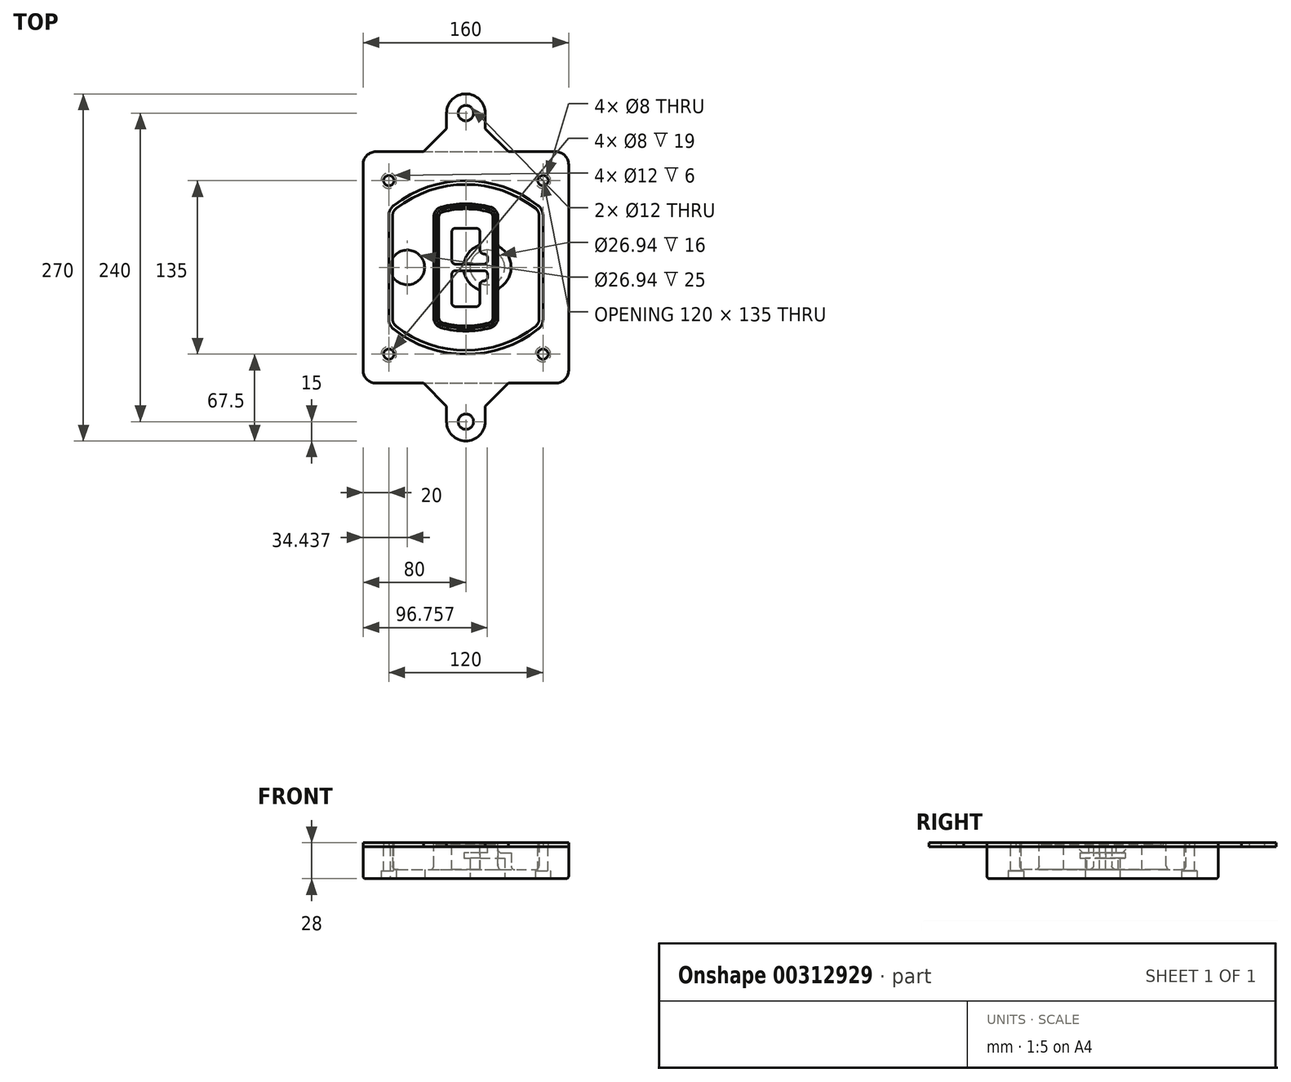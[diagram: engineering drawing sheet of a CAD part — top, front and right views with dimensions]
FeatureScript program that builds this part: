
annotation { "Feature Type Name" : "Feature", "Feature Type Description" : "" }
export const myFeature = defineFeature(function(context is Context, id is Id, definition is map)
    precondition{}
    {
        {
            var Q0;
            Q0=qCreatedBy(makeId("Top.planeOp"),FACE);
            var sketch = newSketch(context, id + "F0", { "sketchPlane" : qUnion([Q0])});
            skPoint(sketch, "E0.rect.middle", {"position": v(0, 0) * mm});
            skLineSegment(sketch, "E1.bottom", {"start": v(-70, -90) * mm, "end": v(70, -90) * mm});
            skLineSegment(sketch, "E1.top", {"start": v(-70, 90) * mm, "end": v(70, 90) * mm});
            skLineSegment(sketch, "E1.left", {"start": v(-80, -80) * mm, "end": v(-80, 80) * mm});
            skLineSegment(sketch, "E1.right", {"start": v(80, -80) * mm, "end": v(80, 80) * mm});
            skLineSegment(sketch, "E2", {"start": v(-80, 90) * mm, "end": v(80, -90) * mm, "construction": true});
            skLineSegment(sketch, "E3", {"start": v(80, 90) * mm, "end": v(-80, -90) * mm, "construction": true});
            skCircle(sketch, "E4", {"center": v(-60, 67.5) * mm, "radius": 4 * mm});
            skCircle(sketch, "E5", {"center": v(60, 67.5) * mm, "radius": 4 * mm});
            skCircle(sketch, "E6", {"center": v(60, -67.5) * mm, "radius": 4 * mm});
            skCircle(sketch, "E7", {"center": v(-60, -67.5) * mm, "radius": 4 * mm});
            skLineSegment(sketch, "E8", {"start": v(-60, 67.5) * mm, "end": v(60, 67.5) * mm, "construction": true});
            skLineSegment(sketch, "E9", {"start": v(60, 67.5) * mm, "end": v(60, -67.5) * mm, "construction": true});
            skLineSegment(sketch, "E10", {"start": v(60, -67.5) * mm, "end": v(-60, -67.5) * mm, "construction": true});
            skLineSegment(sketch, "E11", {"start": v(-60, -67.5) * mm, "end": v(-60, 67.5) * mm, "construction": true});
            skLineSegment(sketch, "E12", {"start": v(-60, 40.3) * mm, "end": v(-60, -40.3) * mm});
            skLineSegment(sketch, "E13", {"start": v(60, 40.3) * mm, "end": v(60, -40.3) * mm});
            skArc(sketch, "E14", {"start": v(56.15, 48.18) * mm, "mid": v(0, 67.5) * mm, "end": v(-56.15, 48.18) * mm});
            skArc(sketch, "E15", {"start": v(-56.15, -48.18) * mm, "mid": v(0, -67.5) * mm, "end": v(56.15, -48.18) * mm});
            skLineSegment(sketch, "E16", {"start": v(-60, 0) * mm, "end": v(60, 0) * mm, "construction": true});
            skPoint(sketch, "E17.visualSharp", {"position": v(-60, -45) * mm});
            skArc(sketch, "E17.filletArc", {"start": v(-60, -40.3) * mm, "mid": v(-58.99, -44.68) * mm, "end": v(-56.15, -48.18) * mm});
            skPoint(sketch, "E18.visualSharp", {"position": v(-60, 45) * mm});
            skArc(sketch, "E18.filletArc", {"start": v(-56.15, 48.18) * mm, "mid": v(-58.99, 44.68) * mm, "end": v(-60, 40.3) * mm});
            skPoint(sketch, "E19.visualSharp", {"position": v(60, 45) * mm});
            skArc(sketch, "E19.filletArc", {"start": v(60, 40.3) * mm, "mid": v(58.99, 44.68) * mm, "end": v(56.15, 48.18) * mm});
            skPoint(sketch, "E20.visualSharp", {"position": v(60, -45) * mm});
            skArc(sketch, "E20.filletArc", {"start": v(56.15, -48.18) * mm, "mid": v(58.99, -44.68) * mm, "end": v(60, -40.3) * mm});
            skPoint(sketch, "E21.visualSharp", {"position": v(-80, 90) * mm});
            skArc(sketch, "E21.filletArc", {"start": v(-70, 90) * mm, "mid": v(-77.07, 87.07) * mm, "end": v(-80, 80) * mm});
            skPoint(sketch, "E22.visualSharp", {"position": v(80, 90) * mm});
            skArc(sketch, "E22.filletArc", {"start": v(80, 80) * mm, "mid": v(77.07, 87.07) * mm, "end": v(70, 90) * mm});
            skPoint(sketch, "E23.visualSharp", {"position": v(80, -90) * mm});
            skArc(sketch, "E23.filletArc", {"start": v(70, -90) * mm, "mid": v(77.07, -87.07) * mm, "end": v(80, -80) * mm});
            skPoint(sketch, "E24.visualSharp", {"position": v(-80, -90) * mm});
            skArc(sketch, "E24.filletArc", {"start": v(-80, -80) * mm, "mid": v(-77.07, -87.07) * mm, "end": v(-70, -90) * mm});
            skArc(sketch, "E25.0", {"start": v(57, 40.3) * mm, "mid": v(56.3, 43.36) * mm, "end": v(54.3, 45.81) * mm});
            skLineSegment(sketch, "E25.1", {"start": v(57, 40.3) * mm, "end": v(57, -40.3) * mm});
            skArc(sketch, "E25.2", {"start": v(54.3, -45.81) * mm, "mid": v(56.3, -43.36) * mm, "end": v(57, -40.3) * mm});
            skArc(sketch, "E25.3", {"start": v(-54.3, -45.81) * mm, "mid": v(0, -64.5) * mm, "end": v(54.3, -45.81) * mm});
            skArc(sketch, "E25.4", {"start": v(-57, -40.3) * mm, "mid": v(-56.3, -43.36) * mm, "end": v(-54.3, -45.81) * mm});
            skArc(sketch, "E25.5", {"start": v(54.3, 45.81) * mm, "mid": v(0, 64.5) * mm, "end": v(-54.3, 45.81) * mm});
            skLineSegment(sketch, "E25.6", {"start": v(-57, 40.3) * mm, "end": v(-57, -40.3) * mm});
            skArc(sketch, "E25.7", {"start": v(-54.3, 45.81) * mm, "mid": v(-56.3, 43.36) * mm, "end": v(-57, 40.3) * mm});
            skArc(sketch, "E26.0", {"start": v(-58.62, 51.33) * mm, "mid": v(-62.58, 46.43) * mm, "end": v(-64, 40.3) * mm});
            skArc(sketch, "E26.1", {"start": v(58.62, 51.33) * mm, "mid": v(0, 71.5) * mm, "end": v(-58.62, 51.33) * mm});
            skArc(sketch, "E26.2", {"start": v(64, 40.3) * mm, "mid": v(62.58, 46.43) * mm, "end": v(58.62, 51.33) * mm});
            skLineSegment(sketch, "E26.3", {"start": v(64, 40.3) * mm, "end": v(64, -40.3) * mm});
            skArc(sketch, "E26.4", {"start": v(58.62, -51.33) * mm, "mid": v(62.58, -46.43) * mm, "end": v(64, -40.3) * mm});
            skLineSegment(sketch, "E26.5", {"start": v(-64, 40.3) * mm, "end": v(-64, -40.3) * mm});
            skArc(sketch, "E26.6", {"start": v(-58.62, -51.33) * mm, "mid": v(0, -71.5) * mm, "end": v(58.62, -51.33) * mm});
            skArc(sketch, "E26.7", {"start": v(-64, -40.3) * mm, "mid": v(-62.58, -46.43) * mm, "end": v(-58.62, -51.33) * mm});
            skSolve(sketch);
        }
        {
            var Q0;
            Q0=makeQuery(id+"F0.imprint","IMPRINT",FACE,{"disambiguationData":[TD([[makeQuery(id+"F0.imprint","IMPRINT",EDGE,{"derivedFrom":sQuery(id+"F0.wireOp",EDGE,"E1.bottom")}),1.0]])]});
            var Q1;
            Q1=makeQuery(id+"F0.imprint","IMPRINT",FACE,{"disambiguationData":[TD([[makeQuery(id+"F0.imprint","IMPRINT",EDGE,{"derivedFrom":sQuery(id+"F0.wireOp",EDGE,"E12")}),1.0]])]});
            var Q2;
            Q2=makeQuery(id+"F0.imprint","IMPRINT",FACE,{"disambiguationData":[TD([[makeQuery(id+"F0.imprint","IMPRINT",EDGE,{"derivedFrom":sQuery(id+"F0.wireOp",EDGE,"E25.0")}),1.0]])]});
            var Q3;
            Q3=makeQuery(id+"F0.imprint","IMPRINT",FACE,{"disambiguationData":[TD([[makeQuery(id+"F0.imprint","IMPRINT",EDGE,{"derivedFrom":sQuery(id+"F0.wireOp",EDGE,"E12")}),-1.0]])]});
            extrude(context, id + "F1", {"entities" : qUnion([Q0, Q1, Q2, Q3]), "oppositeDirection" : true, "depth" : 25 * mm});
        }
        {
            var Q0;
            Q0=makeQuery(id+"F0.imprint","IMPRINT",FACE,{"disambiguationData":[TD([[makeQuery(id+"F0.imprint","IMPRINT",EDGE,{"derivedFrom":sQuery(id+"F0.wireOp",EDGE,"E12")}),1.0]])]});
            extrude(context, id + "F2", {"entities" : qUnion([Q0]), "operationType" : NewBodyOperationType.ADD, "depth" : 3 * mm});
        }
        {
            var Q0;
            Q0=makeQuery(id+"F0.imprint","IMPRINT",FACE,{"disambiguationData":[TD([[makeQuery(id+"F0.imprint","IMPRINT",EDGE,{"derivedFrom":sQuery(id+"F0.wireOp",EDGE,"E25.0")}),1.0]])]});
            extrude(context, id + "F3", {"entities" : qUnion([Q0]), "operationType" : NewBodyOperationType.REMOVE, "oppositeDirection" : true, "depth" : 18 * mm});
        }
        {
            var Q0;
            Q0=makeQuery(id+"F2.opExtrude","CAP_FACE",FACE,{"disambiguationData":[OSD([sQuery(id+"F0.wireOp",EDGE,"E12"),sQuery(id+"F0.wireOp",EDGE,"E13"),sQuery(id+"F0.wireOp",EDGE,"E14"),sQuery(id+"F0.wireOp",EDGE,"E15"),sQuery(id+"F0.wireOp",EDGE,"E17.filletArc"),sQuery(id+"F0.wireOp",EDGE,"E18.filletArc"),sQuery(id+"F0.wireOp",EDGE,"E19.filletArc"),sQuery(id+"F0.wireOp",EDGE,"E20.filletArc"),sQuery(id+"F0.wireOp",EDGE,"E25.0"),sQuery(id+"F0.wireOp",EDGE,"E25.1"),sQuery(id+"F0.wireOp",EDGE,"E25.2"),sQuery(id+"F0.wireOp",EDGE,"E25.3"),sQuery(id+"F0.wireOp",EDGE,"E25.4"),sQuery(id+"F0.wireOp",EDGE,"E25.5"),sQuery(id+"F0.wireOp",EDGE,"E25.6"),sQuery(id+"F0.wireOp",EDGE,"E25.7")])],"isStart":false});
            var sketch = newSketch(context, id + "F4", { "sketchPlane" : qUnion([Q0])});
            skArc(sketch, "E27.0", {"start": v(-19.08, -46.97) * mm, "mid": v(0, -49.5) * mm, "end": v(19.08, -46.97) * mm});
            skArc(sketch, "E28.0", {"start": v(19.08, 46.97) * mm, "mid": v(0, 49.5) * mm, "end": v(-19.08, 46.97) * mm});
            skLineSegment(sketch, "E29", {"start": v(-25, 39.25) * mm, "end": v(-25, -39.25) * mm});
            skLineSegment(sketch, "E30", {"start": v(25, 39.25) * mm, "end": v(25, -39.25) * mm});
            skLineSegment(sketch, "E31", {"start": v(-25, 45.1) * mm, "end": v(25, 45.1) * mm, "construction": true});
            skLineSegment(sketch, "E32", {"start": v(-25, -45.1) * mm, "end": v(25, -45.1) * mm, "construction": true});
            skPoint(sketch, "E33.visualSharp", {"position": v(-25, 45.1) * mm});
            skArc(sketch, "E33.filletArc", {"start": v(-19.08, 46.97) * mm, "mid": v(-23.35, 44.11) * mm, "end": v(-25, 39.25) * mm});
            skPoint(sketch, "E34.visualSharp", {"position": v(25, 45.1) * mm});
            skArc(sketch, "E34.filletArc", {"start": v(25, 39.25) * mm, "mid": v(23.35, 44.11) * mm, "end": v(19.08, 46.97) * mm});
            skPoint(sketch, "E35.visualSharp", {"position": v(25, -45.1) * mm});
            skArc(sketch, "E35.filletArc", {"start": v(19.08, -46.97) * mm, "mid": v(23.35, -44.11) * mm, "end": v(25, -39.25) * mm});
            skPoint(sketch, "E36.visualSharp", {"position": v(-25, -45.1) * mm});
            skArc(sketch, "E36.filletArc", {"start": v(-25, -39.25) * mm, "mid": v(-23.35, -44.11) * mm, "end": v(-19.08, -46.97) * mm});
            skArc(sketch, "E37.0", {"start": v(54.3, 45.81) * mm, "mid": v(0, 64.5) * mm, "end": v(-54.3, 45.81) * mm});
            skArc(sketch, "E37.1", {"start": v(-54.3, 45.81) * mm, "mid": v(-56.3, 43.36) * mm, "end": v(-57, 40.3) * mm});
            skLineSegment(sketch, "E37.2", {"start": v(-57, 40.3) * mm, "end": v(-57, -40.3) * mm});
            skArc(sketch, "E37.3", {"start": v(-57, -40.3) * mm, "mid": v(-56.3, -43.36) * mm, "end": v(-54.3, -45.81) * mm});
            skArc(sketch, "E37.4", {"start": v(-54.3, -45.81) * mm, "mid": v(0, -64.5) * mm, "end": v(54.3, -45.81) * mm});
            skArc(sketch, "E37.5", {"start": v(54.3, -45.81) * mm, "mid": v(56.3, -43.36) * mm, "end": v(57, -40.3) * mm});
            skLineSegment(sketch, "E37.6", {"start": v(57, 40.3) * mm, "end": v(57, -40.3) * mm});
            skArc(sketch, "E37.7", {"start": v(57, 40.3) * mm, "mid": v(56.3, 43.36) * mm, "end": v(54.3, 45.81) * mm});
            skLineSegment(sketch, "E38.0", {"start": v(23, 39.25) * mm, "end": v(23, -39.25) * mm});
            skArc(sketch, "E38.1", {"start": v(18.56, -45.04) * mm, "mid": v(21.76, -42.9) * mm, "end": v(23, -39.25) * mm});
            skArc(sketch, "E38.2", {"start": v(-18.56, -45.04) * mm, "mid": v(0, -47.5) * mm, "end": v(18.56, -45.04) * mm});
            skArc(sketch, "E38.3", {"start": v(-23, -39.25) * mm, "mid": v(-21.76, -42.9) * mm, "end": v(-18.56, -45.04) * mm});
            skLineSegment(sketch, "E38.4", {"start": v(-23, 39.25) * mm, "end": v(-23, -39.25) * mm});
            skArc(sketch, "E38.5", {"start": v(23, 39.25) * mm, "mid": v(21.76, 42.9) * mm, "end": v(18.56, 45.04) * mm});
            skArc(sketch, "E38.6", {"start": v(-18.56, 45.04) * mm, "mid": v(-21.76, 42.9) * mm, "end": v(-23, 39.25) * mm});
            skArc(sketch, "E38.7", {"start": v(18.56, 45.04) * mm, "mid": v(0, 47.5) * mm, "end": v(-18.56, 45.04) * mm});
            skArc(sketch, "E39.0", {"start": v(21, 39.25) * mm, "mid": v(20.18, 41.68) * mm, "end": v(18.04, 43.1) * mm});
            skLineSegment(sketch, "E39.1", {"start": v(21, 39.25) * mm, "end": v(21, -39.25) * mm});
            skArc(sketch, "E39.2", {"start": v(18.04, -43.1) * mm, "mid": v(20.18, -41.68) * mm, "end": v(21, -39.25) * mm});
            skArc(sketch, "E39.3", {"start": v(-18.04, -43.1) * mm, "mid": v(0, -45.5) * mm, "end": v(18.04, -43.1) * mm});
            skArc(sketch, "E39.4", {"start": v(-21, -39.25) * mm, "mid": v(-20.18, -41.68) * mm, "end": v(-18.04, -43.1) * mm});
            skArc(sketch, "E39.5", {"start": v(18.04, 43.1) * mm, "mid": v(0, 45.5) * mm, "end": v(-18.04, 43.1) * mm});
            skLineSegment(sketch, "E39.6", {"start": v(-21, 39.25) * mm, "end": v(-21, -39.25) * mm});
            skArc(sketch, "E39.7", {"start": v(-18.04, 43.1) * mm, "mid": v(-20.18, 41.68) * mm, "end": v(-21, 39.25) * mm});
            skLineSegment(sketch, "E40", {"start": v(-25, 0) * mm, "end": v(25, 0) * mm, "construction": true});
            skLineSegment(sketch, "E41", {"start": v(-11, 5.5) * mm, "end": v(-11, 27.5) * mm});
            skLineSegment(sketch, "E42", {"start": v(-8, 30.5) * mm, "end": v(8, 30.5) * mm});
            skLineSegment(sketch, "E43", {"start": v(11, 27.5) * mm, "end": v(11, 13.5) * mm});
            skLineSegment(sketch, "E44", {"start": v(14, 10.5) * mm, "end": v(14, 10.5) * mm});
            skLineSegment(sketch, "E45", {"start": v(17, 7.5) * mm, "end": v(17, 5.5) * mm});
            skLineSegment(sketch, "E46", {"start": v(14, 2.5) * mm, "end": v(-8, 2.5) * mm});
            skPoint(sketch, "E47.visualSharp", {"position": v(-11, 30.5) * mm});
            skArc(sketch, "E47.filletArc", {"start": v(-8, 30.5) * mm, "mid": v(-10.12, 29.62) * mm, "end": v(-11, 27.5) * mm});
            skPoint(sketch, "E48.visualSharp", {"position": v(11, 30.5) * mm});
            skArc(sketch, "E48.filletArc", {"start": v(11, 27.5) * mm, "mid": v(10.12, 29.62) * mm, "end": v(8, 30.5) * mm});
            skPoint(sketch, "E49.visualSharp", {"position": v(11, 10.5) * mm});
            skArc(sketch, "E49.filletArc", {"start": v(11, 13.5) * mm, "mid": v(11.88, 11.38) * mm, "end": v(14, 10.5) * mm});
            skPoint(sketch, "E50.visualSharp", {"position": v(17, 10.5) * mm});
            skArc(sketch, "E50.filletArc", {"start": v(17, 7.5) * mm, "mid": v(16.12, 9.62) * mm, "end": v(14, 10.5) * mm});
            skPoint(sketch, "E51.visualSharp", {"position": v(17, 2.5) * mm});
            skArc(sketch, "E51.filletArc", {"start": v(14, 2.5) * mm, "mid": v(16.12, 3.38) * mm, "end": v(17, 5.5) * mm});
            skPoint(sketch, "E52.visualSharp", {"position": v(-11, 2.5) * mm});
            skArc(sketch, "E52.filletArc", {"start": v(-11, 5.5) * mm, "mid": v(-10.12, 3.38) * mm, "end": v(-8, 2.5) * mm});
            skLineSegment(sketch, "E53.0.MirrorCS", {"start": v(14, -2.5) * mm, "end": v(-8, -2.5) * mm});
            skArc(sketch, "E54.0.MirrorCS", {"start": v(-11, -5.5) * mm, "mid": v(-10.12, -3.38) * mm, "end": v(-8, -2.5) * mm});
            skLineSegment(sketch, "E55.0.MirrorCS", {"start": v(-11, -5.5) * mm, "end": v(-11, -27.5) * mm});
            skArc(sketch, "E56.0.MirrorCS", {"start": v(-8, -30.5) * mm, "mid": v(-10.12, -29.62) * mm, "end": v(-11, -27.5) * mm});
            skLineSegment(sketch, "E57.0.MirrorCS", {"start": v(-8, -30.5) * mm, "end": v(8, -30.5) * mm});
            skArc(sketch, "E58.0.MirrorCS", {"start": v(11, -27.5) * mm, "mid": v(10.12, -29.62) * mm, "end": v(8, -30.5) * mm});
            skLineSegment(sketch, "E59.0.MirrorCS", {"start": v(11, -27.5) * mm, "end": v(11, -13.5) * mm});
            skArc(sketch, "E60.0.MirrorCS", {"start": v(11, -13.5) * mm, "mid": v(11.88, -11.38) * mm, "end": v(14, -10.5) * mm});
            skArc(sketch, "E61.0.MirrorCS", {"start": v(17, -7.5) * mm, "mid": v(16.12, -9.62) * mm, "end": v(14, -10.5) * mm});
            skLineSegment(sketch, "E62.0.MirrorCS", {"start": v(17, -7.5) * mm, "end": v(17, -5.5) * mm});
            skArc(sketch, "E63.0.MirrorCS", {"start": v(14, -2.5) * mm, "mid": v(16.12, -3.38) * mm, "end": v(17, -5.5) * mm});
            skSolve(sketch);
        }
        {
            var Q0;
            Q0=makeQuery(id+"F4.imprint","IMPRINT",FACE,{"disambiguationData":[TD([[makeQuery(id+"F4.imprint","IMPRINT",EDGE,{"derivedFrom":sQuery(id+"F4.wireOp",EDGE,"E27.0")}),1.0]])]});
            var Q1;
            Q1=makeQuery(id+"F4.imprint","IMPRINT",FACE,{"disambiguationData":[TD([[makeQuery(id+"F4.imprint","IMPRINT",EDGE,{"derivedFrom":sQuery(id+"F4.wireOp",EDGE,"E38.0")}),-1.0]])]});
            var Q2;
            Q2=makeQuery(id+"F4.imprint","IMPRINT",FACE,{"disambiguationData":[TD([[makeQuery(id+"F4.imprint","IMPRINT",EDGE,{"derivedFrom":sQuery(id+"F4.wireOp",EDGE,"E39.0")}),1.0]])]});
            extrude(context, id + "F5", {"entities" : qUnion([Q0, Q1, Q2]), "operationType" : NewBodyOperationType.ADD, "endBound" : BoundingType.UP_TO_NEXT, "oppositeDirection" : true, "depth" : 25 * mm});
        }
        {
            var Q0;
            Q0=makeQuery(id+"F4.imprint","IMPRINT",FACE,{"disambiguationData":[TD([[makeQuery(id+"F4.imprint","IMPRINT",EDGE,{"derivedFrom":sQuery(id+"F4.wireOp",EDGE,"E38.0")}),-1.0]])]});
            extrude(context, id + "F6", {"entities" : qUnion([Q0]), "operationType" : NewBodyOperationType.REMOVE, "oppositeDirection" : true, "depth" : 2 * mm});
        }
        {
            var Q0;
            Q0=makeQuery(id+"F1.opExtrude","CAP_FACE",FACE,{"disambiguationData":[OSD([sQuery(id+"F0.wireOp",EDGE,"E1.bottom"),sQuery(id+"F0.wireOp",EDGE,"E1.top"),sQuery(id+"F0.wireOp",EDGE,"E1.left"),sQuery(id+"F0.wireOp",EDGE,"E1.right"),sQuery(id+"F0.wireOp",EDGE,"E4"),sQuery(id+"F0.wireOp",EDGE,"E5"),sQuery(id+"F0.wireOp",EDGE,"E6"),sQuery(id+"F0.wireOp",EDGE,"E7"),sQuery(id+"F0.wireOp",EDGE,"E21.filletArc"),sQuery(id+"F0.wireOp",EDGE,"E22.filletArc"),sQuery(id+"F0.wireOp",EDGE,"E23.filletArc"),sQuery(id+"F0.wireOp",EDGE,"E24.filletArc")])],"isStart":false});
            var sketch = newSketch(context, id + "F7", { "sketchPlane" : qUnion([Q0])});
            skCircle(sketch, "E64", {"center": v(16.76, 0) * mm, "radius": 13.47 * mm});
            skCircle(sketch, "E65", {"center": v(-45.56, 0) * mm, "radius": 13.47 * mm});
            skLineSegment(sketch, "E66", {"start": v(80, 0) * mm, "end": v(-80, 0) * mm});
            skCircle(sketch, "E67", {"center": v(16.76, 0) * mm, "radius": 18.47 * mm});
            skCircle(sketch, "E68", {"center": v(60, -67.5) * mm, "radius": 6 * mm});
            skCircle(sketch, "E69", {"center": v(-60, -67.5) * mm, "radius": 6 * mm});
            skCircle(sketch, "E70", {"center": v(-60, 67.5) * mm, "radius": 6 * mm});
            skCircle(sketch, "E71", {"center": v(60, 67.5) * mm, "radius": 6 * mm});
            skSolve(sketch);
        }
        {
            var Q0;
            {var subQ1=sQuery(id+"F7.wireOp",EDGE,"E66");var subQ4=sQuery(id+"F7.wireOp",EDGE,"E64");var subQ6=makeQuery(id+"F7.imprint","INTERSECT",VERTEX,{"disambiguationData":[OD(0.0)],"derivedFrom":[subQ4,subQ1]});Q0=makeQuery(id+"F7.imprint","IMPRINT",FACE,{"disambiguationData":[TD([[makeQuery(id+"F7.imprint","IMPRINT",EDGE,{"disambiguationData":[TD([[subQ6,-1.0]])],"derivedFrom":subQ4}),-1.0]])]});}
            var Q1;
            {var subQ0=sQuery(id+"F7.wireOp",EDGE,"E66");var subQ1=sQuery(id+"F7.wireOp",EDGE,"E64");var subQ3=makeQuery(id+"F7.imprint","INTERSECT",VERTEX,{"disambiguationData":[OD(0.0)],"derivedFrom":[subQ1,subQ0]});Q1=makeQuery(id+"F7.imprint","IMPRINT",FACE,{"disambiguationData":[TD([[makeQuery(id+"F7.imprint","IMPRINT",EDGE,{"disambiguationData":[TD([[subQ3,-1.0]])],"derivedFrom":subQ1}),1.0]])]});}
            var Q2;
            {var subQ0=sQuery(id+"F7.wireOp",EDGE,"E66");var subQ1=sQuery(id+"F7.wireOp",EDGE,"E64");var subQ3=makeQuery(id+"F7.imprint","INTERSECT",VERTEX,{"disambiguationData":[OD(0.0)],"derivedFrom":[subQ1,subQ0]});Q2=makeQuery(id+"F7.imprint","IMPRINT",FACE,{"disambiguationData":[TD([[makeQuery(id+"F7.imprint","IMPRINT",EDGE,{"disambiguationData":[TD([[subQ3,1.0]])],"derivedFrom":subQ1}),1.0]])]});}
            var Q3;
            {var subQ1=sQuery(id+"F7.wireOp",EDGE,"E66");var subQ4=sQuery(id+"F7.wireOp",EDGE,"E64");var subQ6=makeQuery(id+"F7.imprint","INTERSECT",VERTEX,{"disambiguationData":[OD(0.0)],"derivedFrom":[subQ4,subQ1]});Q3=makeQuery(id+"F7.imprint","IMPRINT",FACE,{"disambiguationData":[TD([[makeQuery(id+"F7.imprint","IMPRINT",EDGE,{"disambiguationData":[TD([[subQ6,1.0]])],"derivedFrom":subQ4}),-1.0]])]});}
            extrude(context, id + "F8", {"entities" : qUnion([Q0, Q1, Q2, Q3]), "operationType" : NewBodyOperationType.ADD, "oppositeDirection" : true, "depth" : 20 * mm});
        }
        {
            var Q0;
            {var subQ0=sQuery(id+"F7.wireOp",EDGE,"E66");var subQ1=sQuery(id+"F7.wireOp",EDGE,"E64");var subQ3=makeQuery(id+"F7.imprint","INTERSECT",VERTEX,{"disambiguationData":[OD(0.0)],"derivedFrom":[subQ1,subQ0]});Q0=makeQuery(id+"F7.imprint","IMPRINT",FACE,{"disambiguationData":[TD([[makeQuery(id+"F7.imprint","IMPRINT",EDGE,{"disambiguationData":[TD([[subQ3,-1.0]])],"derivedFrom":subQ1}),1.0]])]});}
            var Q1;
            {var subQ0=sQuery(id+"F7.wireOp",EDGE,"E66");var subQ1=sQuery(id+"F7.wireOp",EDGE,"E64");var subQ3=makeQuery(id+"F7.imprint","INTERSECT",VERTEX,{"disambiguationData":[OD(0.0)],"derivedFrom":[subQ1,subQ0]});Q1=makeQuery(id+"F7.imprint","IMPRINT",FACE,{"disambiguationData":[TD([[makeQuery(id+"F7.imprint","IMPRINT",EDGE,{"disambiguationData":[TD([[subQ3,1.0]])],"derivedFrom":subQ1}),1.0]])]});}
            extrude(context, id + "F9", {"entities" : qUnion([Q0, Q1]), "operationType" : NewBodyOperationType.REMOVE, "oppositeDirection" : true, "depth" : 16 * mm});
        }
        {
            var Q0;
            {var subQ0=sQuery(id+"F7.wireOp",EDGE,"E66");var subQ1=sQuery(id+"F7.wireOp",EDGE,"E65");var subQ3=makeQuery(id+"F7.imprint","INTERSECT",VERTEX,{"disambiguationData":[OD(0.0)],"derivedFrom":[subQ1,subQ0]});Q0=makeQuery(id+"F7.imprint","IMPRINT",FACE,{"disambiguationData":[TD([[makeQuery(id+"F7.imprint","IMPRINT",EDGE,{"disambiguationData":[TD([[subQ3,-1.0]])],"derivedFrom":subQ1}),1.0]])]});}
            var Q1;
            {var subQ0=sQuery(id+"F7.wireOp",EDGE,"E66");var subQ1=sQuery(id+"F7.wireOp",EDGE,"E65");var subQ3=makeQuery(id+"F7.imprint","INTERSECT",VERTEX,{"disambiguationData":[OD(0.0)],"derivedFrom":[subQ1,subQ0]});Q1=makeQuery(id+"F7.imprint","IMPRINT",FACE,{"disambiguationData":[TD([[makeQuery(id+"F7.imprint","IMPRINT",EDGE,{"disambiguationData":[TD([[subQ3,1.0]])],"derivedFrom":subQ1}),1.0]])]});}
            extrude(context, id + "F10", {"entities" : qUnion([Q0, Q1]), "operationType" : NewBodyOperationType.REMOVE, "oppositeDirection" : true, "depth" : 25 * mm});
        }
        {
            var Q0;
            Q0=makeQuery(id+"F7.imprint","IMPRINT",FACE,{"disambiguationData":[TD([[makeQuery(id+"F7.imprint","IMPRINT",EDGE,{"derivedFrom":sQuery(id+"F7.wireOp",EDGE,"E68")}),1.0]])]});
            var Q1;
            Q1=makeQuery(id+"F7.imprint","IMPRINT",FACE,{"disambiguationData":[TD([[makeQuery(id+"F7.imprint","IMPRINT",EDGE,{"derivedFrom":makeQuery(id+"F1.opExtrude","CAP_EDGE",EDGE,{"disambiguationData":[OSD([sQuery(id+"F0.wireOp",EDGE,"E5")])],"isStart":false})}),-1.0]])]});
            var Q2;
            Q2=makeQuery(id+"F7.imprint","IMPRINT",FACE,{"disambiguationData":[TD([[makeQuery(id+"F7.imprint","IMPRINT",EDGE,{"derivedFrom":sQuery(id+"F7.wireOp",EDGE,"E69")}),1.0]])]});
            var Q3;
            Q3=makeQuery(id+"F7.imprint","IMPRINT",FACE,{"disambiguationData":[TD([[makeQuery(id+"F7.imprint","IMPRINT",EDGE,{"derivedFrom":makeQuery(id+"F1.opExtrude","CAP_EDGE",EDGE,{"disambiguationData":[OSD([sQuery(id+"F0.wireOp",EDGE,"E4")])],"isStart":false})}),-1.0]])]});
            var Q4;
            Q4=makeQuery(id+"F7.imprint","IMPRINT",FACE,{"disambiguationData":[TD([[makeQuery(id+"F7.imprint","IMPRINT",EDGE,{"derivedFrom":sQuery(id+"F7.wireOp",EDGE,"E70")}),1.0]])]});
            var Q5;
            Q5=makeQuery(id+"F7.imprint","IMPRINT",FACE,{"disambiguationData":[TD([[makeQuery(id+"F7.imprint","IMPRINT",EDGE,{"derivedFrom":makeQuery(id+"F1.opExtrude","CAP_EDGE",EDGE,{"disambiguationData":[OSD([sQuery(id+"F0.wireOp",EDGE,"E7")])],"isStart":false})}),-1.0]])]});
            var Q6;
            Q6=makeQuery(id+"F7.imprint","IMPRINT",FACE,{"disambiguationData":[TD([[makeQuery(id+"F7.imprint","IMPRINT",EDGE,{"derivedFrom":sQuery(id+"F7.wireOp",EDGE,"E71")}),1.0]])]});
            var Q7;
            Q7=makeQuery(id+"F7.imprint","IMPRINT",FACE,{"disambiguationData":[TD([[makeQuery(id+"F7.imprint","IMPRINT",EDGE,{"derivedFrom":makeQuery(id+"F1.opExtrude","CAP_EDGE",EDGE,{"disambiguationData":[OSD([sQuery(id+"F0.wireOp",EDGE,"E6")])],"isStart":false})}),-1.0]])]});
            extrude(context, id + "F11", {"entities" : qUnion([Q0, Q1, Q2, Q3, Q4, Q5, Q6, Q7]), "operationType" : NewBodyOperationType.REMOVE, "oppositeDirection" : true, "depth" : 6 * mm});
        }
        {
            var Q0;
            Q0=makeQuery(id+"F9.boolean.opBoolean","COPY",FACE,{"derivedFrom":makeQuery(id+"F9.opExtrude","CAP_FACE",FACE,{"disambiguationData":[OSD([sQuery(id+"F7.wireOp",EDGE,"E64")])],"isStart":false})});
            var sketch = newSketch(context, id + "F12", { "sketchPlane" : qUnion([Q0])});
            skArc(sketch, "E72.0", {"start": v(11, 17.55) * mm, "mid": v(2.57, 11.82) * mm, "end": v(-1.54, 2.5) * mm});
            skArc(sketch, "E72.1", {"start": v(-1.54, -2.5) * mm, "mid": v(2.57, -11.82) * mm, "end": v(11, -17.55) * mm});
            skLineSegment(sketch, "E73", {"start": v(-1.54, -2.5) * mm, "end": v(14, -2.5) * mm});
            skLineSegment(sketch, "E74.0", {"start": v(14, 2.5) * mm, "end": v(-1.54, 2.5) * mm});
            skArc(sketch, "E74.1", {"start": v(14, 2.5) * mm, "mid": v(16.12, 3.38) * mm, "end": v(17, 5.5) * mm});
            skLineSegment(sketch, "E74.2", {"start": v(17, 7.5) * mm, "end": v(17, 5.5) * mm});
            skArc(sketch, "E74.3", {"start": v(17, 7.5) * mm, "mid": v(16.12, 9.62) * mm, "end": v(14, 10.5) * mm});
            skArc(sketch, "E74.4", {"start": v(11, 13.5) * mm, "mid": v(11.88, 11.38) * mm, "end": v(14, 10.5) * mm});
            skLineSegment(sketch, "E74.5", {"start": v(11, 17.55) * mm, "end": v(11, 13.5) * mm});
            skLineSegment(sketch, "E74.7", {"start": v(14, -2.5) * mm, "end": v(-1.54, -2.5) * mm});
            skArc(sketch, "E74.8", {"start": v(14, -2.5) * mm, "mid": v(16.12, -3.38) * mm, "end": v(17, -5.5) * mm});
            skLineSegment(sketch, "E74.9", {"start": v(17, -7.5) * mm, "end": v(17, -5.5) * mm});
            skArc(sketch, "E74.10", {"start": v(17, -7.5) * mm, "mid": v(16.12, -9.62) * mm, "end": v(14, -10.5) * mm});
            skArc(sketch, "E74.11", {"start": v(11, -13.5) * mm, "mid": v(11.88, -11.38) * mm, "end": v(14, -10.5) * mm});
            skLineSegment(sketch, "E74.12", {"start": v(11, -17.55) * mm, "end": v(11, -13.5) * mm});
            skPoint(sketch, "E75.orphan", {"position": v(11, -27.5) * mm});
            skPoint(sketch, "E76.orphan", {"position": v(-8, -2.5) * mm});
            skPoint(sketch, "E77.orphan", {"position": v(-8, 2.5) * mm});
            skPoint(sketch, "E78.orphan", {"position": v(11, 27.5) * mm});
            skSolve(sketch);
        }
        {
            var Q0;
            {var subQ7=sQuery(id+"F12.wireOp",EDGE,"E72.0");var subQ14=sQuery(id+"F12.wireOp",EDGE,"E72.1");var subQ16=sQuery(id+"F12.wireOp",EDGE,"E74.1");var subQ18=sQuery(id+"F12.wireOp",EDGE,"E74.8");Q0=qUnion([makeQuery(id+"F12.imprint","IMPRINT",FACE,{"disambiguationData":[TD([[makeQuery(id+"F12.imprint","IMPRINT",EDGE,{"derivedFrom":subQ7}),1.0]])]}),makeQuery(id+"F12.imprint","IMPRINT",FACE,{"disambiguationData":[TD([[makeQuery(id+"F12.imprint","IMPRINT",EDGE,{"derivedFrom":subQ14}),1.0]])]}),makeQuery(id+"F12.imprint","IMPRINT",FACE,{"disambiguationData":[TD([[makeQuery(id+"F12.imprint","IMPRINT",EDGE,{"derivedFrom":subQ16}),1.0]])]}),makeQuery(id+"F12.imprint","IMPRINT",FACE,{"disambiguationData":[TD([[makeQuery(id+"F12.imprint","IMPRINT",EDGE,{"derivedFrom":subQ18}),-1.0]])]})]);}
            var Q1;
            Q1=makeQuery(id+"F5.boolean.opBoolean","SPLIT",FACE,{"disambiguationData":[TD([makeQuery(id+"F5.opExtrude","SWEPT_FACE",FACE,{"disambiguationData":[OSD([sQuery(id+"F4.wireOp",EDGE,"E41")])]})])],"derivedFrom":makeQuery(id+"F3.boolean.opBoolean","COPY",FACE,{"derivedFrom":makeQuery(id+"F3.opExtrude","CAP_FACE",FACE,{"disambiguationData":[OSD([sQuery(id+"F0.wireOp",EDGE,"E25.0"),sQuery(id+"F0.wireOp",EDGE,"E25.1"),sQuery(id+"F0.wireOp",EDGE,"E25.2"),sQuery(id+"F0.wireOp",EDGE,"E25.3"),sQuery(id+"F0.wireOp",EDGE,"E25.4"),sQuery(id+"F0.wireOp",EDGE,"E25.5"),sQuery(id+"F0.wireOp",EDGE,"E25.6"),sQuery(id+"F0.wireOp",EDGE,"E25.7")])],"isStart":false})})});
            extrude(context, id + "F13", {"entities" : qUnion([Q0]), "operationType" : NewBodyOperationType.REMOVE, "endBound" : BoundingType.UP_TO_SURFACE, "endBoundEntityFace" : qUnion([Q1]), "depth" : 25 * mm});
        }
        {
            var Q0;
            Q0=makeQuery(id+"F3.boolean.opBoolean","COPY",EDGE,{"derivedFrom":makeQuery(id+"F3.opExtrude","CAP_EDGE",EDGE,{"disambiguationData":[OSD([sQuery(id+"F0.wireOp",EDGE,"E25.6")])],"isStart":false})});
            var Q1;
            Q1=makeQuery(id+"F8.boolean.opBoolean","INTERSECT",EDGE,{"derivedFrom":[makeQuery(id+"F5.opExtrude","SWEPT_FACE",FACE,{"disambiguationData":[OSD([sQuery(id+"F4.wireOp",EDGE,"E30")])]}),makeQuery(id+"F8.opExtrude","CAP_FACE",FACE,{"disambiguationData":[OSD([sQuery(id+"F7.wireOp",EDGE,"E67")])],"isStart":false})]});
            var Q2;
            Q2=makeQuery(id+"F8.boolean.opBoolean","INTERSECT",EDGE,{"disambiguationData":[OD(1.0)],"derivedFrom":[makeQuery(id+"F5.opExtrude","SWEPT_FACE",FACE,{"disambiguationData":[OSD([sQuery(id+"F4.wireOp",EDGE,"E30")])]}),makeQuery(id+"F8.opExtrude","SWEPT_FACE",FACE,{"disambiguationData":[OSD([sQuery(id+"F7.wireOp",EDGE,"E67")])]})]});
            var Q3;
            {var subQ0=sQuery(id+"F4.wireOp",EDGE,"E30");Q3=makeQuery(id+"F8.boolean.opBoolean","SPLIT",EDGE,{"disambiguationData":[TD([makeQuery(id+"F5.opExtrude","SWEPT_FACE",FACE,{"disambiguationData":[OSD([sQuery(id+"F4.wireOp",EDGE,"E35.filletArc")])]})])],"derivedFrom":makeQuery(id+"F5.opExtrude","CAP_EDGE",EDGE,{"disambiguationData":[OSD([subQ0])],"isStart":false})});}
            var Q4;
            {var subQ0=sQuery(id+"F0.wireOp",EDGE,"E25.7");var subQ1=sQuery(id+"F0.wireOp",EDGE,"E25.1");var subQ2=sQuery(id+"F0.wireOp",EDGE,"E25.6");var subQ3=sQuery(id+"F0.wireOp",EDGE,"E25.5");var subQ4=sQuery(id+"F0.wireOp",EDGE,"E25.4");var subQ5=sQuery(id+"F0.wireOp",EDGE,"E25.0");var subQ6=sQuery(id+"F0.wireOp",EDGE,"E25.2");var subQ7=sQuery(id+"F0.wireOp",EDGE,"E25.3");Q4=makeQuery(id+"F8.boolean.opBoolean","INTERSECT",EDGE,{"derivedFrom":[makeQuery(id+"F5.boolean.opBoolean","SPLIT",FACE,{"disambiguationData":[TD([makeQuery(id+"F2.opExtrude","SWEPT_FACE",FACE,{"disambiguationData":[OSD([subQ5])]})])],"derivedFrom":makeQuery(id+"F3.boolean.opBoolean","COPY",FACE,{"derivedFrom":makeQuery(id+"F3.opExtrude","CAP_FACE",FACE,{"disambiguationData":[OSD([subQ5,subQ1,subQ6,subQ7,subQ4,subQ3,subQ2,subQ0])],"isStart":false})})}),makeQuery(id+"F8.opExtrude","SWEPT_FACE",FACE,{"disambiguationData":[OSD([sQuery(id+"F7.wireOp",EDGE,"E67")])]})]});}
            var Q5;
            Q5=makeQuery(id+"F8.boolean.opBoolean","INTERSECT",EDGE,{"disambiguationData":[OD(0.0)],"derivedFrom":[makeQuery(id+"F5.opExtrude","SWEPT_FACE",FACE,{"disambiguationData":[OSD([sQuery(id+"F4.wireOp",EDGE,"E30")])]}),makeQuery(id+"F8.opExtrude","SWEPT_FACE",FACE,{"disambiguationData":[OSD([sQuery(id+"F7.wireOp",EDGE,"E67")])]})]});
            fillet(context, id + "F14", {"entities" : qUnion([Q0, Q1, Q2, Q3, Q4, Q5]), "radius" : 3 * mm, "tangentPropagation" : true, "allowEdgeOverflow" : false});
        }
        {
            var Q0;
            Q0=makeQuery(id+"F1.opExtrude","CAP_EDGE",EDGE,{"disambiguationData":[OSD([sQuery(id+"F0.wireOp",EDGE,"E1.bottom")])],"isStart":false});
            fillet(context, id + "F15", {"entities" : qUnion([Q0]), "radius" : 2 * mm, "tangentPropagation" : true, "allowEdgeOverflow" : false});
        }
        {
            var Q0;
            {var subQ0=sQuery(id+"F0.wireOp",EDGE,"E21.filletArc");var subQ1=sQuery(id+"F0.wireOp",EDGE,"E7");var subQ2=sQuery(id+"F0.wireOp",EDGE,"E6");var subQ3=sQuery(id+"F0.wireOp",EDGE,"E5");var subQ4=sQuery(id+"F0.wireOp",EDGE,"E4");var subQ5=sQuery(id+"F0.wireOp",EDGE,"E22.filletArc");var subQ6=sQuery(id+"F0.wireOp",EDGE,"E1.bottom");var subQ7=sQuery(id+"F0.wireOp",EDGE,"E1.right");var subQ8=sQuery(id+"F0.wireOp",EDGE,"E1.top");var subQ9=sQuery(id+"F0.wireOp",EDGE,"E1.left");var subQ10=sQuery(id+"F0.wireOp",EDGE,"E23.filletArc");var subQ11=sQuery(id+"F0.wireOp",EDGE,"E24.filletArc");Q0=makeQuery(id+"F2.boolean.opBoolean","SPLIT",FACE,{"disambiguationData":[TD([makeQuery(id+"F1.opExtrude","SWEPT_FACE",FACE,{"disambiguationData":[OSD([subQ6])]})])],"derivedFrom":makeQuery(id+"F1.opExtrude","CAP_FACE",FACE,{"disambiguationData":[OSD([subQ6,subQ8,subQ9,subQ7,subQ4,subQ3,subQ2,subQ1,subQ0,subQ5,subQ10,subQ11])],"isStart":true})});}
            var sketch = newSketch(context, id + "F16", { "sketchPlane" : qUnion([Q0])});
            skCircle(sketch, "E79", {"center": v(0, 120) * mm, "radius": 6 * mm});
            skArc(sketch, "E80", {"start": v(15, 120) * mm, "mid": v(0, 135) * mm, "end": v(-15, 120) * mm});
            skLineSegment(sketch, "E81", {"start": v(-15, 120) * mm, "end": v(-15, 108) * mm});
            skLineSegment(sketch, "E82", {"start": v(15, 120) * mm, "end": v(15, 108) * mm});
            skLineSegment(sketch, "E83", {"start": v(15, 108) * mm, "end": v(33, 90) * mm});
            skLineSegment(sketch, "E84", {"start": v(-15, 108) * mm, "end": v(-33, 90) * mm});
            skPoint(sketch, "E85.endSnap0", {"position": v(80, 0) * mm});
            skLineSegment(sketch, "E86", {"start": v(-118.63, 0) * mm, "end": v(127.33, 0) * mm});
            skPoint(sketch, "E86.endSnap0", {"position": v(-60, 0) * mm});
            skLineSegment(sketch, "E87.MirrorCS", {"start": v(15, -120) * mm, "end": v(15, -108) * mm});
            skArc(sketch, "E88.MirrorCS", {"start": v(15, -120) * mm, "mid": v(0, -135) * mm, "end": v(-15, -120) * mm});
            skLineSegment(sketch, "E89.MirrorCS", {"start": v(-15, -120) * mm, "end": v(-15, -108) * mm});
            skCircle(sketch, "E90.MirrorC", {"center": v(0, -120) * mm, "radius": 6 * mm});
            skLineSegment(sketch, "E91.MirrorCS", {"start": v(15, -108) * mm, "end": v(33, -90) * mm});
            skLineSegment(sketch, "E92.MirrorCS", {"start": v(-15, -108) * mm, "end": v(-33, -90) * mm});
            skSolve(sketch);
        }
        {
            var Q0;
            Q0=makeQuery(id+"F16.imprint","IMPRINT",FACE,{"disambiguationData":[TD([[makeQuery(id+"F16.imprint","IMPRINT",EDGE,{"derivedFrom":sQuery(id+"F16.wireOp",EDGE,"E79")}),-1.0]])]});
            var Q1;
            Q1=makeQuery(id+"F16.imprint","IMPRINT",FACE,{"disambiguationData":[TD([[makeQuery(id+"F16.imprint","IMPRINT",EDGE,{"derivedFrom":sQuery(id+"F16.wireOp",EDGE,"E87.MirrorCS")}),1.0]])]});
            var Q2;
            Q2=makeQuery(id+"F16.imprint","IMPRINT",FACE,{"disambiguationData":[TD([[makeQuery(id+"F16.imprint","IMPRINT",EDGE,{"derivedFrom":makeQuery(id+"F1.opExtrude","CAP_EDGE",EDGE,{"disambiguationData":[OSD([sQuery(id+"F0.wireOp",EDGE,"E4")])],"isStart":true})}),-1.0]])]});
            var Q3;
            Q3=makeQuery(id+"F16.imprint","IMPRINT",FACE,{"disambiguationData":[TD([[makeQuery(id+"F16.imprint","IMPRINT",EDGE,{"derivedFrom":makeQuery(id+"F1.opExtrude","CAP_EDGE",EDGE,{"disambiguationData":[OSD([sQuery(id+"F0.wireOp",EDGE,"E6")])],"isStart":true})}),-1.0]])]});
            var Q4;
            Q4=makeQuery(id+"F2.opExtrude","CAP_FACE",FACE,{"disambiguationData":[OSD([sQuery(id+"F0.wireOp",EDGE,"E12"),sQuery(id+"F0.wireOp",EDGE,"E13"),sQuery(id+"F0.wireOp",EDGE,"E14"),sQuery(id+"F0.wireOp",EDGE,"E15"),sQuery(id+"F0.wireOp",EDGE,"E17.filletArc"),sQuery(id+"F0.wireOp",EDGE,"E18.filletArc"),sQuery(id+"F0.wireOp",EDGE,"E19.filletArc"),sQuery(id+"F0.wireOp",EDGE,"E20.filletArc"),sQuery(id+"F0.wireOp",EDGE,"E25.0"),sQuery(id+"F0.wireOp",EDGE,"E25.1"),sQuery(id+"F0.wireOp",EDGE,"E25.2"),sQuery(id+"F0.wireOp",EDGE,"E25.3"),sQuery(id+"F0.wireOp",EDGE,"E25.4"),sQuery(id+"F0.wireOp",EDGE,"E25.5"),sQuery(id+"F0.wireOp",EDGE,"E25.6"),sQuery(id+"F0.wireOp",EDGE,"E25.7")])],"isStart":false});
            extrude(context, id + "F17", {"entities" : qUnion([Q0, Q1, Q2, Q3]), "endBound" : BoundingType.UP_TO_SURFACE, "endBoundEntityFace" : qUnion([Q4]), "depth" : 25 * mm});
        }
    });
